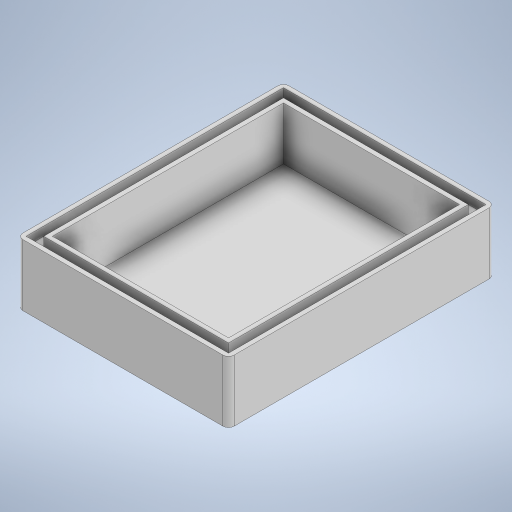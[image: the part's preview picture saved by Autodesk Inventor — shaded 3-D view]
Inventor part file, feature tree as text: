
AUTODESK INVENTOR PART (.ipt)
format: ipt  version: 2024.2 (Build 282272000, 272)  size: 620,032 bytes
history: native  units: in
note: dims shown in document units (in); Inventor stores cm internally (conversion verified against a paired STEP export)
features: extrude x4, sketch x3, projected_geometry x2, fillet x1
ambient origin geometry x8: Origin, YZ Plane, XZ Plane, XY Plane, X Axis, Y Axis, Z Axis, Center Point
bodies: Solid1 (feature_tree)
feature tree (10):
  sketch  "Sketch1"  dims[d0=0.82in d1=0.625in]
  extrude  "Extrusion1"  Depth=0.625in
  extrude  "Extrusion2"  Depth=0.0625in
  extrude  "Extrusion3"  Depth=0.0625in
  extrude  "Extrusion4"  Depth=0.0312in TaperAngle=0.0deg
  fillet  "Fillet1"  Radius=0.2188in
  sketch  "Sketch2"  dims[d2=0.0625in d3=0.0625in]
  projected_geometry  "Projected Loop1"
  sketch  "Sketch3"  dims[d4=0.0625in d5=0.0625in d6=0.0312in d7=0.0in d8=0.2188in d9=0.0in d10=0.125in d11=0.0312in d12=0.2188in d13=0.0in d14=0.0156in d15=0.0156in d16=0.0156in d17=0.0156in d18=0.0156in d19=0.0156in d20=0.0156in d21=0.0156in d22=0.0312in d23=0.0in d24=0.02in d25=0.0344in]
  projected_geometry  "Projected Loop2"
